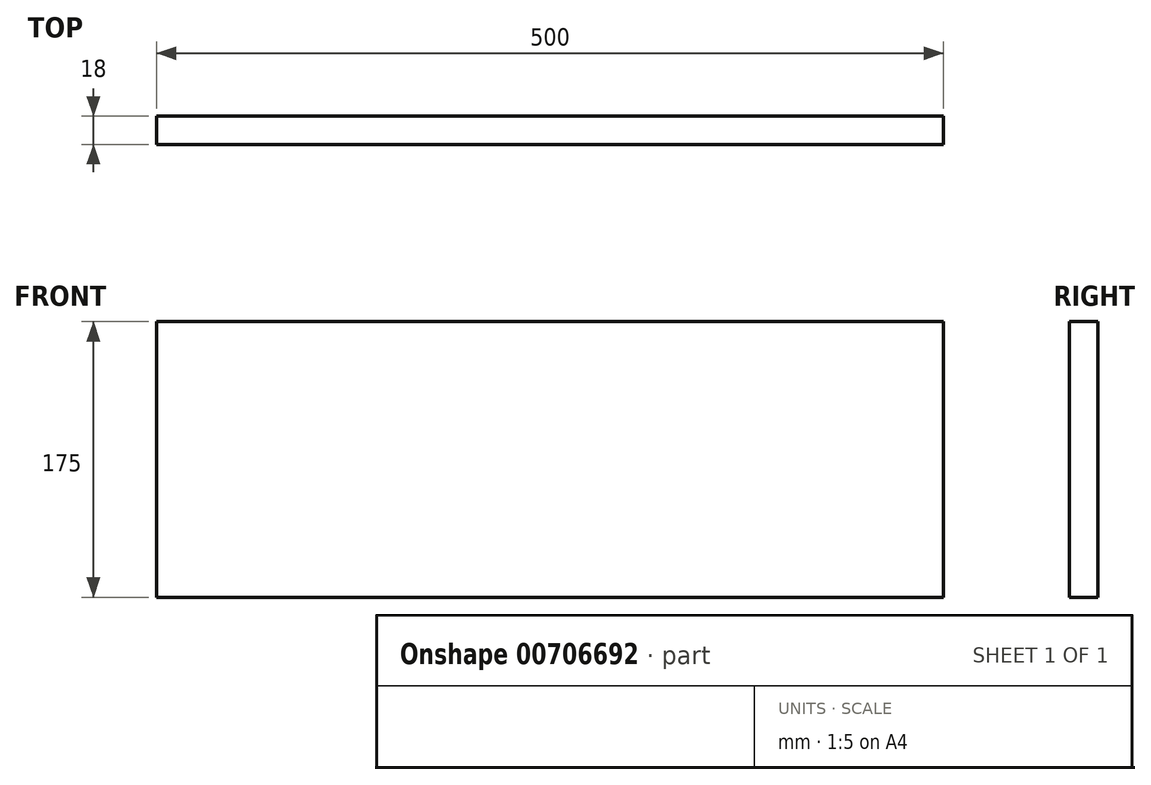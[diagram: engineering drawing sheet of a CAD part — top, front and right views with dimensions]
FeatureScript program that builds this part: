
annotation { "Feature Type Name" : "Feature", "Feature Type Description" : "" }
export const myFeature = defineFeature(function(context is Context, id is Id, definition is map)
    precondition{}
    {
        {
            var Q0;
            Q0=qCreatedBy(makeId("Front.planeOp"),FACE);
            var sketch = newSketch(context, id + "F0", { "sketchPlane" : qUnion([Q0])});
            skLineSegment(sketch, "E0.bottom", {"start": v(-250, -87.5) * mm, "end": v(250, -87.5) * mm});
            skLineSegment(sketch, "E0.top", {"start": v(-250, 87.5) * mm, "end": v(250, 87.5) * mm});
            skLineSegment(sketch, "E0.left", {"start": v(-250, -87.5) * mm, "end": v(-250, 87.5) * mm});
            skLineSegment(sketch, "E0.right", {"start": v(250, -87.5) * mm, "end": v(250, 87.5) * mm});
            skPoint(sketch, "E0.middle", {"position": v(0, 0) * mm});
            skSolve(sketch);
        }
        {
            var Q0;
            Q0=makeQuery(id+"F0.imprint","IMPRINT",FACE,{"disambiguationData":[TD([[makeQuery(id+"F0.imprint","IMPRINT",EDGE,{"derivedFrom":sQuery(id+"F0.wireOp",EDGE,"E0.bottom")}),1.0]])]});
            extrude(context, id + "F1", {"entities" : qUnion([Q0]), "depth" : 18 * mm, "offsetDistance" : 25 * mm, "symmetric" : true});
        }
    });
